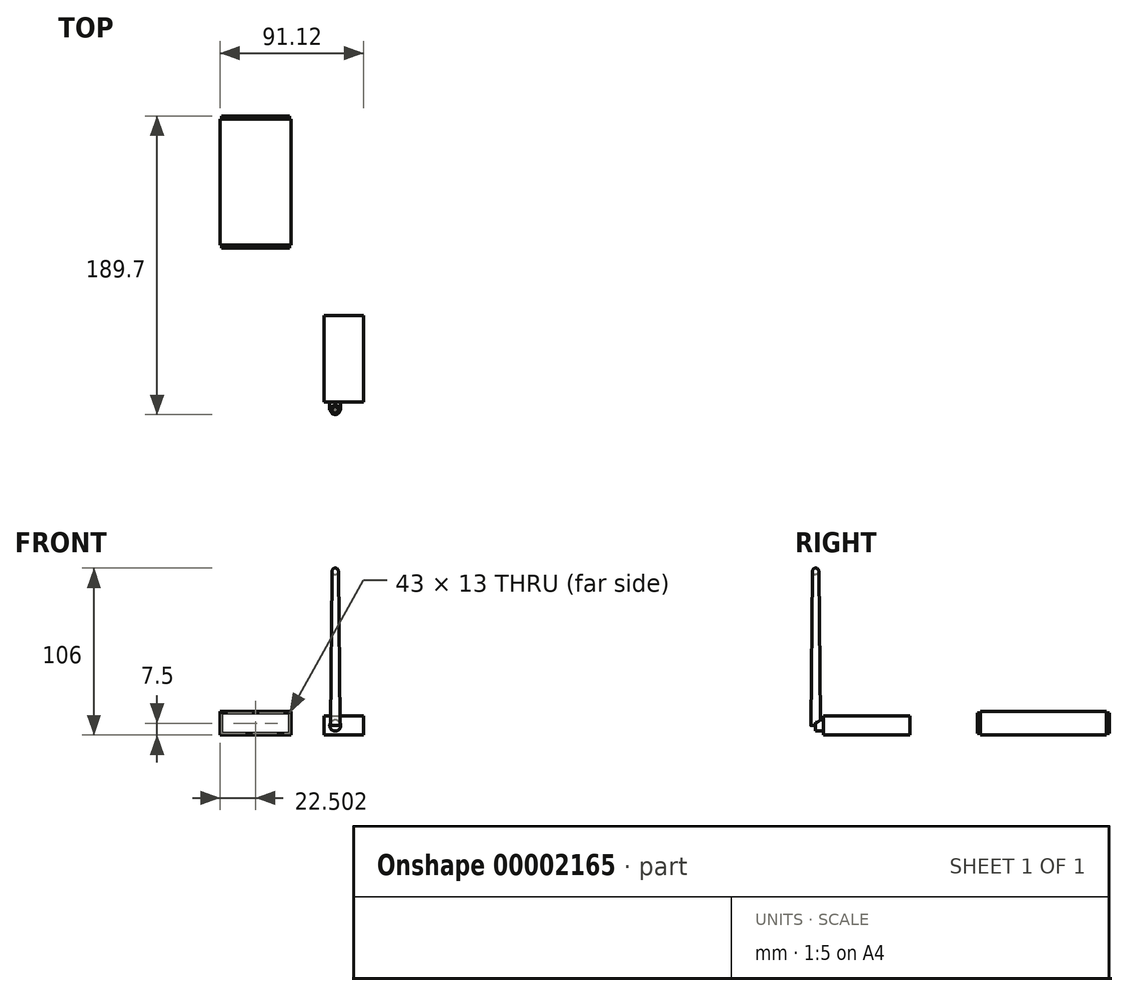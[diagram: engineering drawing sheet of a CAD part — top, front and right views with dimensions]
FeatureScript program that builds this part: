
annotation { "Feature Type Name" : "Feature", "Feature Type Description" : "" }
export const myFeature = defineFeature(function(context is Context, id is Id, definition is map)
    precondition{}
    {
        {
            var Q0;
            Q0=qCreatedBy(makeId("Top.planeOp"),FACE);
            var sketch = newSketch(context, id + "F0", { "sketchPlane" : qUnion([Q0])});
            skLineSegment(sketch, "E0.bottom", {"start": v(-73.12, 96.7) * mm, "end": v(-28.12, 96.7) * mm});
            skLineSegment(sketch, "E0.top", {"start": v(-73.12, 12.7) * mm, "end": v(-28.12, 12.7) * mm});
            skLineSegment(sketch, "E0.left", {"start": v(-73.12, 96.7) * mm, "end": v(-73.12, 12.7) * mm});
            skLineSegment(sketch, "E0.right", {"start": v(-28.12, 96.7) * mm, "end": v(-28.12, 12.7) * mm});
            skSolve(sketch);
        }
        {
            var Q0;
            Q0 = qSketchRegion(id + "F0", true);
            extrude(context, id + "F1", {"entities" : qUnion([Q0]), "depth" : 15 * mm});
        }
        {
            var Q0;
            Q0=makeQuery(id+"F1.opExtrude","SWEPT_FACE",FACE,{"disambiguationData":[OSD([sQuery(id+"F0.wireOp",EDGE,"E0.top")])]});
            var sketch = newSketch(context, id + "F2", { "sketchPlane" : qUnion([Q0])});
            skLineSegment(sketch, "E1.0", {"start": v(-72.12, 14) * mm, "end": v(-29.12, 14) * mm});
            skLineSegment(sketch, "E1.1", {"start": v(-72.12, 14) * mm, "end": v(-72.12, 1) * mm});
            skLineSegment(sketch, "E1.2", {"start": v(-72.12, 1) * mm, "end": v(-29.12, 1) * mm});
            skLineSegment(sketch, "E1.3", {"start": v(-29.12, 14) * mm, "end": v(-29.12, 1) * mm});
            skLineSegment(sketch, "E2.0", {"start": v(-73.12, 15) * mm, "end": v(-28.12, 15) * mm});
            skLineSegment(sketch, "E2.1", {"start": v(-73.12, 15) * mm, "end": v(-73.12, 0) * mm});
            skLineSegment(sketch, "E2.2", {"start": v(-73.12, 0) * mm, "end": v(-28.12, 0) * mm});
            skLineSegment(sketch, "E2.3", {"start": v(-28.12, 15) * mm, "end": v(-28.12, 0) * mm});
            skSolve(sketch);
        }
        {
            var Q0;
            Q0 = qSketchRegion(id + "F2", true);
            extrude(context, id + "F3", {"entities" : qUnion([Q0]), "operationType" : NewBodyOperationType.REMOVE, "oppositeDirection" : true, "depth" : 2 * mm});
        }
        {
            var Q0;
            Q0=makeQuery(id+"F1.opExtrude","SWEPT_FACE",FACE,{"disambiguationData":[OSD([sQuery(id+"F0.wireOp",EDGE,"E0.bottom")])]});
            var sketch = newSketch(context, id + "F4", { "sketchPlane" : qUnion([Q0])});
            skLineSegment(sketch, "E3.0", {"start": v(73.12, 15) * mm, "end": v(73.12, 0) * mm});
            skLineSegment(sketch, "E3.1", {"start": v(73.12, 15) * mm, "end": v(28.12, 15) * mm});
            skLineSegment(sketch, "E3.2", {"start": v(28.12, 15) * mm, "end": v(28.12, 0) * mm});
            skLineSegment(sketch, "E3.3", {"start": v(73.12, 0) * mm, "end": v(28.12, 0) * mm});
            skLineSegment(sketch, "E4.0", {"start": v(72.12, 14) * mm, "end": v(29.12, 14) * mm});
            skLineSegment(sketch, "E4.1", {"start": v(72.12, 14) * mm, "end": v(72.12, 1) * mm});
            skLineSegment(sketch, "E4.2", {"start": v(72.12, 1) * mm, "end": v(29.12, 1) * mm});
            skLineSegment(sketch, "E4.3", {"start": v(29.12, 14) * mm, "end": v(29.12, 1) * mm});
            skSolve(sketch);
        }
        {
            var Q0;
            Q0 = qSketchRegion(id + "F4", true);
            extrude(context, id + "F5", {"entities" : qUnion([Q0]), "operationType" : NewBodyOperationType.REMOVE, "oppositeDirection" : true, "depth" : 2 * mm});
        }
        {
            var Q0;
            Q0=qCreatedBy(makeId("Top.planeOp"),FACE);
            var sketch = newSketch(context, id + "F6", { "sketchPlane" : qUnion([Q0])});
            skLineSegment(sketch, "E5.bottom", {"start": v(-7, -30) * mm, "end": v(18, -30) * mm});
            skLineSegment(sketch, "E5.top", {"start": v(-7, -85) * mm, "end": v(18, -85) * mm});
            skLineSegment(sketch, "E5.left", {"start": v(-7, -30) * mm, "end": v(-7, -85) * mm});
            skLineSegment(sketch, "E5.right", {"start": v(18, -30) * mm, "end": v(18, -85) * mm});
            skLineSegment(sketch, "E6", {"start": v(0, 0) * mm, "end": v(0, -30) * mm, "construction": true});
            skSolve(sketch);
        }
        {
            var Q0;
            Q0 = qSketchRegion(id + "F6", true);
            extrude(context, id + "F7", {"entities" : qUnion([Q0]), "depth" : 12 * mm});
        }
        {
            var Q0;
            Q0=makeQuery(id+"F7.opExtrude","SWEPT_FACE",FACE,{"disambiguationData":[OSD([sQuery(id+"F6.wireOp",EDGE,"E5.top")])]});
            var sketch = newSketch(context, id + "F8", { "sketchPlane" : qUnion([Q0])});
            skLineSegment(sketch, "E7", {"start": v(-7, 6) * mm, "end": v(18, 6) * mm, "construction": true});
            skCircle(sketch, "E8", {"center": v(0, 6) * mm, "radius": 3.5 * mm});
            skSolve(sketch);
        }
        {
            var Q0;
            Q0 = qSketchRegion(id + "F8", true);
            extrude(context, id + "F9", {"entities" : qUnion([Q0]), "operationType" : NewBodyOperationType.ADD, "depth" : 5 * mm});
        }
        {
            var Q0;
            Q0=qCreatedBy(makeId("Right.planeOp"),FACE);
            var sketch = newSketch(context, id + "F10", { "sketchPlane" : qUnion([Q0])});
            skLineSegment(sketch, "E9", {"start": v(-90, 6) * mm, "end": v(-90, 106) * mm});
            skLineSegment(sketch, "E10.0", {"start": v(-90, 2.5) * mm, "end": v(-90, 9.5) * mm, "construction": true});
            skLineSegment(sketch, "E11", {"start": v(-90, 6) * mm, "end": v(-137.04, 6) * mm, "construction": true});
            skLineSegment(sketch, "E12", {"start": v(-92, 104.02) * mm, "end": v(-93, 6) * mm});
            skLineSegment(sketch, "E13", {"start": v(-93, 6) * mm, "end": v(-90, 6) * mm});
            skPoint(sketch, "E14.visualSharp", {"position": v(-91.82, 122) * mm});
            skArc(sketch, "E14.filletArc", {"start": v(-90, 106) * mm, "mid": v(-91.4, 105.42) * mm, "end": v(-92, 104.02) * mm});
            skSolve(sketch);
        }
        {
            var Q0;
            Q0 = qSketchRegion(id + "F10", true);
            var Q1;
            Q1=sQuery(id+"F10.wireOp",EDGE,"E9");
            revolve(context, id + "F11", {"operationType" : NewBodyOperationType.ADD, "entities" : qUnion([Q0]), "axis" : qUnion([Q1]), "revolveType" : RevolveType.FULL});
        }
    });
